# Revit family: O5DR
name_source: partatom
category: Mechanical Equipment
units: mm (PartAtom-declared; Revit-internal decimal feet)

## family parameters
Always vertical = Yes
Cut with Voids When Loaded = No
OmniClass Number = 23.40.40.11.17
OmniClass Title = Refrigerated Cases
Part Type = Normal
Room Calculation Point = No
Round Connector Dimension = Use Radius
Shared = No
Work Plane-Based = Yes

## types (2) — shared parameters
24" Shelf = Yes
Application Discipline = Dairy
BOTTOM ELECTRICAL = Yes
BOTTOM REFRIGERATION PIPING = Yes
BTUH Conventional = 1360
BTUH Parallel = 1190
Certifications = NSF 7, UL471, CSA
DATE = 05/18/2016
DESIGNERS NAME = SHIDDRAMESH
DRAIN LINE = 72"
DRAIN PIPING = Yes
Default Elevation = 48"
Defrosts Per Day = 2
Description = Multi-Deck Merchandiser
Discharge Air (°F) = 32 °F
Discharge Air Velocity (FPM) = 250 FPM
EQUIPMENT DESCRIPTION = Multi-Deck Merchandiser
EQUIPMENT MARK = O5DR
Evaporator (°F) = 28 °F
GLASS = Glass
Height = 81 5/8"
High Efficiency Amps = 1 A
High Efficiency Watts = 67 W
High Power (Cornice) Amps = 0 A
High Power (Cornice) Watts = 30 W
Item Description = Multi-Deck Merchandiser
LF STD END = Yes
Legend Number = O5DR
Length of Cases = 72"
Light Length = 4'
Lights Per Row = 2
Manufacturer = HILL PHOENIX
Model = O5DR
Number of Door = 3
Number of Fans = 4
PAINTED METAL UPPER SHELF = PAINTED SHELVES
REAR REFRIGERATION PIPING = Yes
REFRIGERATION PIPING = COPPER PIPE
RT STD END = Yes
Refgn = 28 5/8"
STAINLESS STEEL = GALVANIZED STEEL
Standard Power Amps = 0 A
Standard Power Watts = 12 W
Superheat Set Point @ Bulb (°F) = 6-8 °F
TOP ELECTRICAL = Yes
TOP REFRIGERATION PIPING = Yes
Timed-Off Defrost Fail-Safe (Min) = 30 (min)
Timed-Off Defrost Termination Temp = 42 °F
URL = http://www.hillphoenix.com
Width = 43 3/8"

## per-type parameters (varying)
| type | CENTER LINE | Length |
| 12' | 72" | 144" |
| 08' | 48" | 96" |

## geometry (parser evidence)
native form markers: Blend x11, Sweep x2
no freeform markers — native parametric forms only
